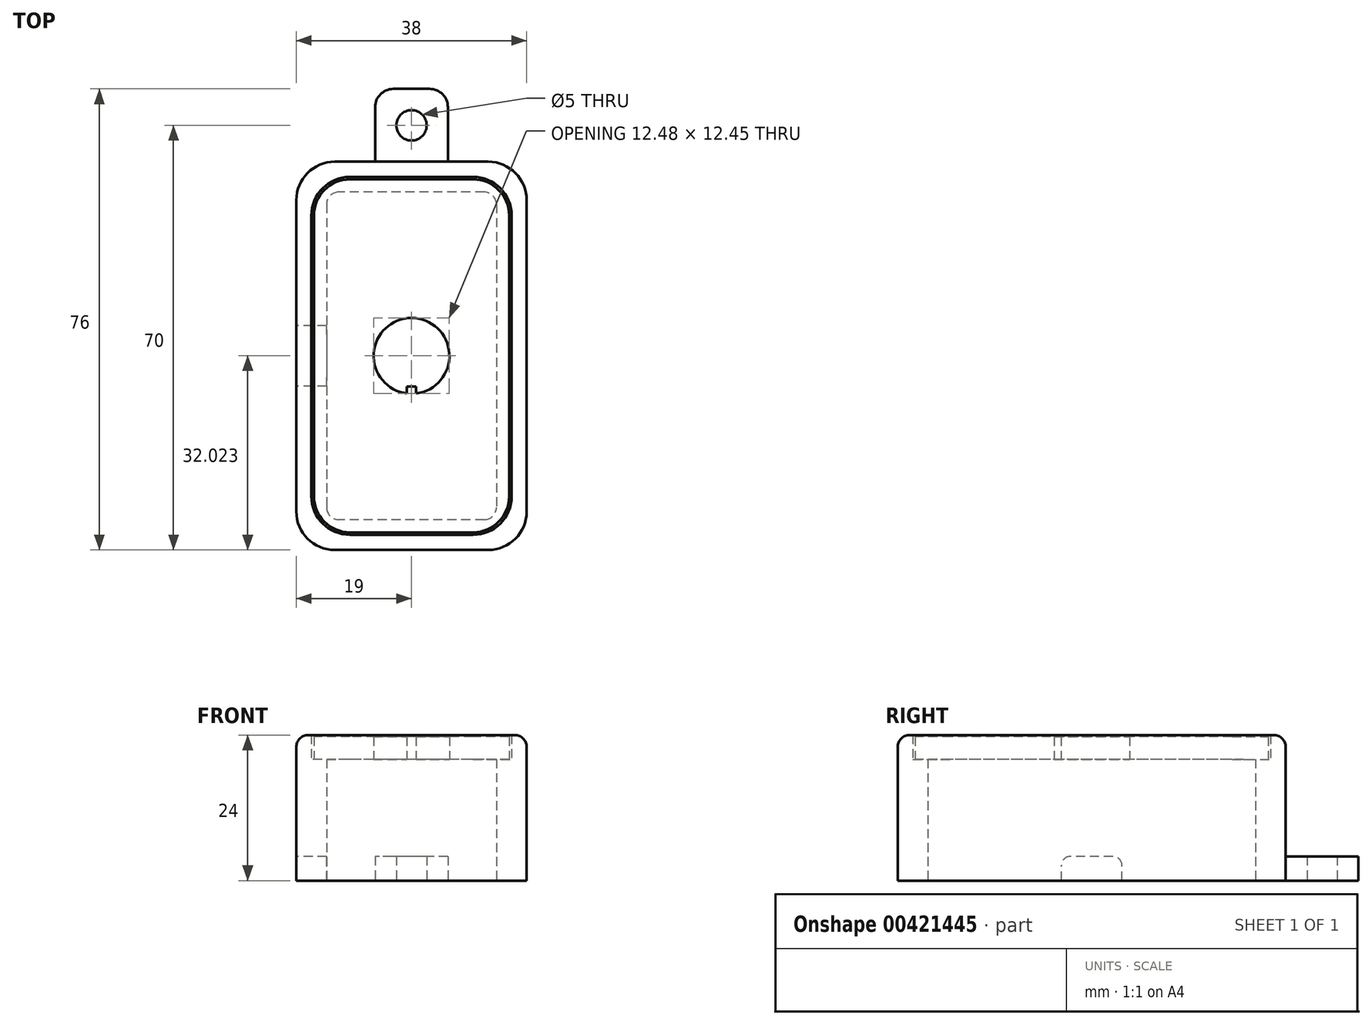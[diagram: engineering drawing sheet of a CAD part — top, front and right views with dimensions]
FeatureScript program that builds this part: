
annotation { "Feature Type Name" : "Feature", "Feature Type Description" : "" }
export const myFeature = defineFeature(function(context is Context, id is Id, definition is map)
    precondition{}
    {
        {
            var Q0;
            Q0=qCreatedBy(makeId("Top.planeOp"),FACE);
            var sketch = newSketch(context, id + "F0", { "sketchPlane" : qUnion([Q0])});
            skLineSegment(sketch, "E0.bottom", {"start": v(12.65, 32) * mm, "end": v(-12.65, 32) * mm});
            skLineSegment(sketch, "E0.top", {"start": v(12.65, -32) * mm, "end": v(-12.65, -32) * mm});
            skLineSegment(sketch, "E0.left", {"start": v(19, 25.65) * mm, "end": v(19, -25.65) * mm});
            skLineSegment(sketch, "E0.right", {"start": v(-19, 25.65) * mm, "end": v(-19, -25.65) * mm});
            skPoint(sketch, "E0.middle", {"position": v(0, 0) * mm});
            skLineSegment(sketch, "E1.0", {"start": v(10.15, 29.5) * mm, "end": v(-10.15, 29.5) * mm});
            skLineSegment(sketch, "E1.1", {"start": v(16.5, 23.15) * mm, "end": v(16.5, -23.15) * mm});
            skLineSegment(sketch, "E1.2", {"start": v(10.15, -29.5) * mm, "end": v(-10.15, -29.5) * mm});
            skLineSegment(sketch, "E1.3", {"start": v(-16.5, 23.15) * mm, "end": v(-16.5, -23.15) * mm});
            skLineSegment(sketch, "E2.0", {"start": v(12, 27) * mm, "end": v(-12, 27) * mm});
            skLineSegment(sketch, "E2.1", {"start": v(14, 25) * mm, "end": v(14, -25) * mm});
            skLineSegment(sketch, "E2.2", {"start": v(12, -27) * mm, "end": v(-12, -27) * mm});
            skLineSegment(sketch, "E2.3", {"start": v(-14, 25) * mm, "end": v(-14, -25) * mm});
            skPoint(sketch, "E3.visualSharp", {"position": v(-19, 32) * mm});
            skArc(sketch, "E3.filletArc", {"start": v(-12.65, 32) * mm, "mid": v(-17.14, 30.14) * mm, "end": v(-19, 25.65) * mm});
            skPoint(sketch, "E4.visualSharp", {"position": v(19, 32) * mm});
            skArc(sketch, "E4.filletArc", {"start": v(19, 25.65) * mm, "mid": v(17.14, 30.14) * mm, "end": v(12.65, 32) * mm});
            skPoint(sketch, "E5.visualSharp", {"position": v(19, -32) * mm});
            skArc(sketch, "E5.filletArc", {"start": v(12.65, -32) * mm, "mid": v(17.14, -30.14) * mm, "end": v(19, -25.65) * mm});
            skPoint(sketch, "E6.visualSharp", {"position": v(-19, -32) * mm});
            skArc(sketch, "E6.filletArc", {"start": v(-19, -25.65) * mm, "mid": v(-17.14, -30.14) * mm, "end": v(-12.65, -32) * mm});
            skPoint(sketch, "E7.visualSharp", {"position": v(-16.5, -29.5) * mm});
            skArc(sketch, "E7.filletArc", {"start": v(-16.5, -23.15) * mm, "mid": v(-14.64, -27.64) * mm, "end": v(-10.15, -29.5) * mm});
            skPoint(sketch, "E8.visualSharp", {"position": v(16.5, -29.5) * mm});
            skArc(sketch, "E8.filletArc", {"start": v(10.15, -29.5) * mm, "mid": v(14.64, -27.64) * mm, "end": v(16.5, -23.15) * mm});
            skPoint(sketch, "E9.visualSharp", {"position": v(16.5, 29.5) * mm});
            skArc(sketch, "E9.filletArc", {"start": v(16.5, 23.15) * mm, "mid": v(14.64, 27.64) * mm, "end": v(10.15, 29.5) * mm});
            skPoint(sketch, "E10.visualSharp", {"position": v(-16.5, 29.5) * mm});
            skArc(sketch, "E10.filletArc", {"start": v(-10.15, 29.5) * mm, "mid": v(-14.64, 27.64) * mm, "end": v(-16.5, 23.15) * mm});
            skLineSegment(sketch, "E11", {"start": v(0, 32) * mm, "end": v(0, 38) * mm, "construction": true});
            skLineSegment(sketch, "E12.bottom", {"start": v(3, 44) * mm, "end": v(-3, 44) * mm});
            skLineSegment(sketch, "E12.top", {"start": v(6, 32) * mm, "end": v(-6, 32) * mm});
            skLineSegment(sketch, "E12.left", {"start": v(6, 41) * mm, "end": v(6, 32) * mm});
            skLineSegment(sketch, "E12.right", {"start": v(-6, 41) * mm, "end": v(-6, 32) * mm});
            skPoint(sketch, "E12.middle", {"position": v(0, 38) * mm});
            skPoint(sketch, "E13.visualSharp", {"position": v(-6, 44) * mm});
            skArc(sketch, "E13.filletArc", {"start": v(-3, 44) * mm, "mid": v(-5.12, 43.12) * mm, "end": v(-6, 41) * mm});
            skPoint(sketch, "E14.visualSharp", {"position": v(6, 44) * mm});
            skArc(sketch, "E14.filletArc", {"start": v(6, 41) * mm, "mid": v(5.12, 43.12) * mm, "end": v(3, 44) * mm});
            skArc(sketch, "E15.MirrorCS", {"start": v(6, -41) * mm, "mid": v(5.12, -43.12) * mm, "end": v(3, -44) * mm});
            skLineSegment(sketch, "E16.MirrorCS", {"start": v(6, -41) * mm, "end": v(6, -32) * mm});
            skLineSegment(sketch, "E17.MirrorCS", {"start": v(3, -44) * mm, "end": v(-3, -44) * mm});
            skArc(sketch, "E18.MirrorCS", {"start": v(-3, -44) * mm, "mid": v(-5.12, -43.12) * mm, "end": v(-6, -41) * mm});
            skLineSegment(sketch, "E19.MirrorCS", {"start": v(-6, -41) * mm, "end": v(-6, -32) * mm});
            skPoint(sketch, "E20.visualSharp", {"position": v(-14, 27) * mm});
            skArc(sketch, "E20.filletArc", {"start": v(-12, 27) * mm, "mid": v(-13.41, 26.41) * mm, "end": v(-14, 25) * mm});
            skPoint(sketch, "E21.visualSharp", {"position": v(14, 27) * mm});
            skArc(sketch, "E21.filletArc", {"start": v(14, 25) * mm, "mid": v(13.41, 26.41) * mm, "end": v(12, 27) * mm});
            skPoint(sketch, "E22.visualSharp", {"position": v(14, -27) * mm});
            skArc(sketch, "E22.filletArc", {"start": v(12, -27) * mm, "mid": v(13.41, -26.41) * mm, "end": v(14, -25) * mm});
            skPoint(sketch, "E23.visualSharp", {"position": v(-14, -27) * mm});
            skArc(sketch, "E23.filletArc", {"start": v(-14, -25) * mm, "mid": v(-13.41, -26.41) * mm, "end": v(-12, -27) * mm});
            skCircle(sketch, "E24", {"center": v(0, 38) * mm, "radius": 2.5 * mm});
            skLineSegment(sketch, "E25", {"start": v(0, -32) * mm, "end": v(0, -38) * mm, "construction": true});
            skCircle(sketch, "E26", {"center": v(0, -38) * mm, "radius": 2.5 * mm});
            skSolve(sketch);
        }
        {
            var Q0;
            Q0=makeQuery(id+"F0.imprint","IMPRINT",FACE,{"disambiguationData":[TD([[makeQuery(id+"F0.imprint","IMPRINT",EDGE,{"derivedFrom":sQuery(id+"F0.wireOp",EDGE,"E0.left")}),-1.0]])]});
            var Q1;
            Q1=makeQuery(id+"F0.imprint","IMPRINT",FACE,{"disambiguationData":[TD([[makeQuery(id+"F0.imprint","IMPRINT",EDGE,{"derivedFrom":sQuery(id+"F0.wireOp",EDGE,"E1.0")}),1.0]])]});
            extrude(context, id + "F1", {"entities" : qUnion([Q0, Q1]), "depth" : 20 * mm});
        }
        {
            var Q0;
            Q0=makeQuery(id+"F0.imprint","IMPRINT",FACE,{"disambiguationData":[TD([[makeQuery(id+"F0.imprint","IMPRINT",EDGE,{"derivedFrom":sQuery(id+"F0.wireOp",EDGE,"E0.left")}),-1.0]])]});
            extrude(context, id + "F2", {"entities" : qUnion([Q0]), "operationType" : NewBodyOperationType.ADD, "depth" : 24 * mm});
        }
        {
            var Q0;
            Q0=makeQuery(id+"F0.imprint","IMPRINT",FACE,{"disambiguationData":[TD([[makeQuery(id+"F0.imprint","IMPRINT",EDGE,{"derivedFrom":sQuery(id+"F0.wireOp",EDGE,"E12.bottom")}),1.0]])]});
            var Q1;
            Q1=makeQuery(id+"F0.imprint","IMPRINT",FACE,{"disambiguationData":[TD([[makeQuery(id+"F0.imprint","IMPRINT",EDGE,{"derivedFrom":sQuery(id+"F0.wireOp",EDGE,"E15.MirrorCS")}),-1.0]])]});
            extrude(context, id + "F3", {"entities" : qUnion([Q0, Q1]), "operationType" : NewBodyOperationType.ADD, "depth" : 4 * mm});
        }
        {
            var Q0;
            {var subQ0=sQuery(id+"F0.wireOp",EDGE,"E12.top");var subQ1=sQuery(id+"F0.wireOp",EDGE,"E0.bottom");Q0=makeQuery(id+"F2.boolean.opBoolean","MERGE",FACE,{"derivedFrom":[makeQuery(id+"F1.opExtrude","SWEPT_FACE",FACE,{"disambiguationData":[OSD([subQ1,subQ0])]}),makeQuery(id+"F2.opExtrude","SWEPT_FACE",FACE,{"disambiguationData":[OSD([subQ1,subQ0])]})]});}
            var sketch = newSketch(context, id + "F4", { "sketchPlane" : qUnion([Q0])});
            skLineSegment(sketch, "E27.bottom", {"start": v(8, 0) * mm, "end": v(12, 0) * mm});
            skLineSegment(sketch, "E27.top", {"start": v(9.5, 4) * mm, "end": v(10.5, 4) * mm});
            skLineSegment(sketch, "E27.left", {"start": v(8, 0) * mm, "end": v(8, 2.5) * mm});
            skLineSegment(sketch, "E27.right", {"start": v(12, 0) * mm, "end": v(12, 2.5) * mm});
            skLineSegment(sketch, "E28.0", {"start": v(6, 4) * mm, "end": v(6, 0) * mm});
            skPoint(sketch, "E29.visualSharp", {"position": v(8, 4) * mm});
            skArc(sketch, "E29.filletArc", {"start": v(9.5, 4) * mm, "mid": v(8.44, 3.56) * mm, "end": v(8, 2.5) * mm});
            skPoint(sketch, "E30.visualSharp", {"position": v(12, 4) * mm});
            skArc(sketch, "E30.filletArc", {"start": v(12, 2.5) * mm, "mid": v(11.56, 3.56) * mm, "end": v(10.5, 4) * mm});
            skSolve(sketch);
        }
        {
            var Q0;
            Q0=makeQuery(id+"F2.opExtrude","CAP_EDGE",EDGE,{"disambiguationData":[OSD([sQuery(id+"F0.wireOp",EDGE,"E0.right")])],"isStart":false});
            var Q1;
            Q1=makeQuery(id+"F2.opExtrude","CAP_EDGE",EDGE,{"disambiguationData":[OSD([sQuery(id+"F0.wireOp",EDGE,"E3.filletArc")])],"isStart":false});
            var Q2;
            Q2=makeQuery(id+"F2.opExtrude","CAP_EDGE",EDGE,{"disambiguationData":[OSD([sQuery(id+"F0.wireOp",EDGE,"E0.bottom"),sQuery(id+"F0.wireOp",EDGE,"E12.top")])],"isStart":false});
            var Q3;
            Q3=makeQuery(id+"F2.opExtrude","CAP_EDGE",EDGE,{"disambiguationData":[OSD([sQuery(id+"F0.wireOp",EDGE,"E4.filletArc")])],"isStart":false});
            var Q4;
            Q4=makeQuery(id+"F2.opExtrude","CAP_EDGE",EDGE,{"disambiguationData":[OSD([sQuery(id+"F0.wireOp",EDGE,"E0.left")])],"isStart":false});
            var Q5;
            Q5=makeQuery(id+"F2.opExtrude","CAP_EDGE",EDGE,{"disambiguationData":[OSD([sQuery(id+"F0.wireOp",EDGE,"E5.filletArc")])],"isStart":false});
            var Q6;
            Q6=makeQuery(id+"F2.opExtrude","CAP_EDGE",EDGE,{"disambiguationData":[OSD([sQuery(id+"F0.wireOp",EDGE,"E0.top")])],"isStart":false});
            var Q7;
            Q7=makeQuery(id+"F2.opExtrude","CAP_EDGE",EDGE,{"disambiguationData":[OSD([sQuery(id+"F0.wireOp",EDGE,"E6.filletArc")])],"isStart":false});
            fillet(context, id + "F5", {"entities" : qUnion([Q0, Q1, Q2, Q3, Q4, Q5, Q6, Q7]), "radius" : 2 * mm, "tangentPropagation" : true, "allowEdgeOverflow" : false});
        }
        {
            var Q0;
            Q0=makeQuery(id+"F1.opExtrude","CAP_FACE",FACE,{"disambiguationData":[OSD([sQuery(id+"F0.wireOp",EDGE,"E0.bottom"),sQuery(id+"F0.wireOp",EDGE,"E0.top"),sQuery(id+"F0.wireOp",EDGE,"E0.left"),sQuery(id+"F0.wireOp",EDGE,"E0.right"),sQuery(id+"F0.wireOp",EDGE,"E2.0"),sQuery(id+"F0.wireOp",EDGE,"E2.1"),sQuery(id+"F0.wireOp",EDGE,"E2.2"),sQuery(id+"F0.wireOp",EDGE,"E2.3"),sQuery(id+"F0.wireOp",EDGE,"E3.filletArc"),sQuery(id+"F0.wireOp",EDGE,"E4.filletArc"),sQuery(id+"F0.wireOp",EDGE,"E5.filletArc"),sQuery(id+"F0.wireOp",EDGE,"E6.filletArc"),sQuery(id+"F0.wireOp",EDGE,"E12.top"),sQuery(id+"F0.wireOp",EDGE,"E20.filletArc"),sQuery(id+"F0.wireOp",EDGE,"E21.filletArc"),sQuery(id+"F0.wireOp",EDGE,"E22.filletArc"),sQuery(id+"F0.wireOp",EDGE,"E23.filletArc")])],"isStart":false});
            var sketch = newSketch(context, id + "F6", { "sketchPlane" : qUnion([Q0])});
            skArc(sketch, "E31.0", {"start": v(-10.15, 29.5) * mm, "mid": v(-14.64, 27.64) * mm, "end": v(-16.5, 23.15) * mm});
            skLineSegment(sketch, "E31.1", {"start": v(10.15, 29.5) * mm, "end": v(-10.15, 29.5) * mm});
            skArc(sketch, "E31.2", {"start": v(16.5, 23.15) * mm, "mid": v(14.64, 27.64) * mm, "end": v(10.15, 29.5) * mm});
            skLineSegment(sketch, "E31.3", {"start": v(16.5, 23.15) * mm, "end": v(16.5, -23.15) * mm});
            skArc(sketch, "E31.4", {"start": v(10.15, -29.5) * mm, "mid": v(14.64, -27.64) * mm, "end": v(16.5, -23.15) * mm});
            skLineSegment(sketch, "E31.5", {"start": v(10.15, -29.5) * mm, "end": v(-10.15, -29.5) * mm});
            skArc(sketch, "E31.6", {"start": v(-16.5, -23.15) * mm, "mid": v(-14.64, -27.64) * mm, "end": v(-10.15, -29.5) * mm});
            skLineSegment(sketch, "E31.7", {"start": v(-16.5, 23.15) * mm, "end": v(-16.5, -23.15) * mm});
            skArc(sketch, "E32.0", {"start": v(16.1, 23.15) * mm, "mid": v(14.36, 27.36) * mm, "end": v(10.15, 29.1) * mm});
            skLineSegment(sketch, "E32.1", {"start": v(16.1, 23.15) * mm, "end": v(16.1, -23.15) * mm});
            skLineSegment(sketch, "E32.2", {"start": v(10.15, 29.1) * mm, "end": v(-10.15, 29.1) * mm});
            skArc(sketch, "E32.3", {"start": v(10.15, -29.1) * mm, "mid": v(14.36, -27.36) * mm, "end": v(16.1, -23.15) * mm});
            skArc(sketch, "E32.4", {"start": v(-10.15, 29.1) * mm, "mid": v(-14.36, 27.36) * mm, "end": v(-16.1, 23.15) * mm});
            skLineSegment(sketch, "E32.5", {"start": v(-16.1, 23.15) * mm, "end": v(-16.1, -23.15) * mm});
            skArc(sketch, "E32.6", {"start": v(-16.1, -23.15) * mm, "mid": v(-14.36, -27.36) * mm, "end": v(-10.15, -29.1) * mm});
            skLineSegment(sketch, "E32.7", {"start": v(10.15, -29.1) * mm, "end": v(-10.15, -29.1) * mm});
            skCircle(sketch, "E33", {"center": v(0, 0) * mm, "radius": 6.25 * mm});
            skPoint(sketch, "E34", {"position": v(6.25, 0) * mm});
            skLineSegment(sketch, "E35.bottom", {"start": v(5.05, 0.75) * mm, "end": v(7.45, 0.75) * mm});
            skLineSegment(sketch, "E35.top", {"start": v(5.05, -0.75) * mm, "end": v(7.45, -0.75) * mm});
            skLineSegment(sketch, "E35.left", {"start": v(5.05, 0.75) * mm, "end": v(5.05, -0.75) * mm});
            skLineSegment(sketch, "E35.right", {"start": v(7.45, 0.75) * mm, "end": v(7.45, -0.75) * mm});
            skPoint(sketch, "E36", {"position": v(0, -6.25) * mm});
            skLineSegment(sketch, "E37.bottom", {"start": v(0.75, -5.05) * mm, "end": v(-0.75, -5.05) * mm});
            skLineSegment(sketch, "E37.top", {"start": v(0.75, -7.45) * mm, "end": v(-0.75, -7.45) * mm});
            skLineSegment(sketch, "E37.left", {"start": v(0.75, -5.05) * mm, "end": v(0.75, -7.45) * mm});
            skLineSegment(sketch, "E37.right", {"start": v(-0.75, -5.05) * mm, "end": v(-0.75, -7.45) * mm});
            skSolve(sketch);
        }
        {
            var Q0;
            Q0=makeQuery(id+"F6.imprint","IMPRINT",FACE,{"disambiguationData":[TD([[makeQuery(id+"F6.imprint","IMPRINT",EDGE,{"derivedFrom":sQuery(id+"F6.wireOp",EDGE,"E32.0")}),1.0]])]});
            var Q1;
            Q1=makeQuery(id+"F6.imprint","IMPRINT",FACE,{"disambiguationData":[TD([[makeQuery(id+"F6.imprint","IMPRINT",EDGE,{"derivedFrom":makeQuery(id+"F1.opExtrude","CAP_EDGE",EDGE,{"disambiguationData":[OSD([sQuery(id+"F0.wireOp",EDGE,"E2.0")])],"isStart":false})}),1.0]])]});
            var Q2;
            {var subQ5=sQuery(id+"F6.wireOp",EDGE,"E35.right");Q2=makeQuery(id+"F6.imprint","IMPRINT",FACE,{"disambiguationData":[TD([[makeQuery(id+"F6.imprint","IMPRINT",EDGE,{"derivedFrom":subQ5}),-1.0]])]});}
            var Q3;
            {var subQ5=sQuery(id+"F6.wireOp",EDGE,"E37.bottom");Q3=makeQuery(id+"F6.imprint","IMPRINT",FACE,{"disambiguationData":[TD([[makeQuery(id+"F6.imprint","IMPRINT",EDGE,{"derivedFrom":subQ5}),1.0]])]});}
            var Q4;
            {var subQ5=sQuery(id+"F6.wireOp",EDGE,"E37.top");Q4=makeQuery(id+"F6.imprint","IMPRINT",FACE,{"disambiguationData":[TD([[makeQuery(id+"F6.imprint","IMPRINT",EDGE,{"derivedFrom":subQ5}),-1.0]])]});}
            extrude(context, id + "F7", {"entities" : qUnion([Q0, Q1, Q2, Q3, Q4]), "depth" : 3.7 * mm});
        }
        {
            var Q0;
            {var subQ0=sQuery(id+"F0.wireOp",EDGE,"E0.right");Q0=makeQuery(id+"F2.boolean.opBoolean","MERGE",FACE,{"derivedFrom":[makeQuery(id+"F1.opExtrude","SWEPT_FACE",FACE,{"disambiguationData":[OSD([subQ0])]}),makeQuery(id+"F2.opExtrude","SWEPT_FACE",FACE,{"disambiguationData":[OSD([subQ0])]})]});}
            var sketch = newSketch(context, id + "F8", { "sketchPlane" : qUnion([Q0])});
            skLineSegment(sketch, "E38.bottom", {"start": v(-5, 0) * mm, "end": v(5, 0) * mm});
            skLineSegment(sketch, "E38.top", {"start": v(-3.5, 4) * mm, "end": v(3.5, 4) * mm});
            skLineSegment(sketch, "E38.left", {"start": v(-5, 0) * mm, "end": v(-5, 2.5) * mm});
            skLineSegment(sketch, "E38.right", {"start": v(5, 0) * mm, "end": v(5, 2.5) * mm});
            skPoint(sketch, "E39", {"position": v(0, 0) * mm});
            skPoint(sketch, "E40.visualSharp", {"position": v(-5, 4) * mm});
            skArc(sketch, "E40.filletArc", {"start": v(-3.5, 4) * mm, "mid": v(-4.56, 3.56) * mm, "end": v(-5, 2.5) * mm});
            skPoint(sketch, "E41.visualSharp", {"position": v(5, 4) * mm});
            skArc(sketch, "E41.filletArc", {"start": v(5, 2.5) * mm, "mid": v(4.56, 3.56) * mm, "end": v(3.5, 4) * mm});
            skSolve(sketch);
        }
        {
            var Q0;
            Q0=makeQuery(id+"F8.imprint","IMPRINT",FACE,{"disambiguationData":[TD([[makeQuery(id+"F8.imprint","IMPRINT",EDGE,{"derivedFrom":sQuery(id+"F8.wireOp",EDGE,"E38.bottom")}),1.0]])]});
            extrude(context, id + "F9", {"entities" : qUnion([Q0]), "operationType" : NewBodyOperationType.REMOVE, "oppositeDirection" : true, "depth" : 5 * mm});
        }
    });
